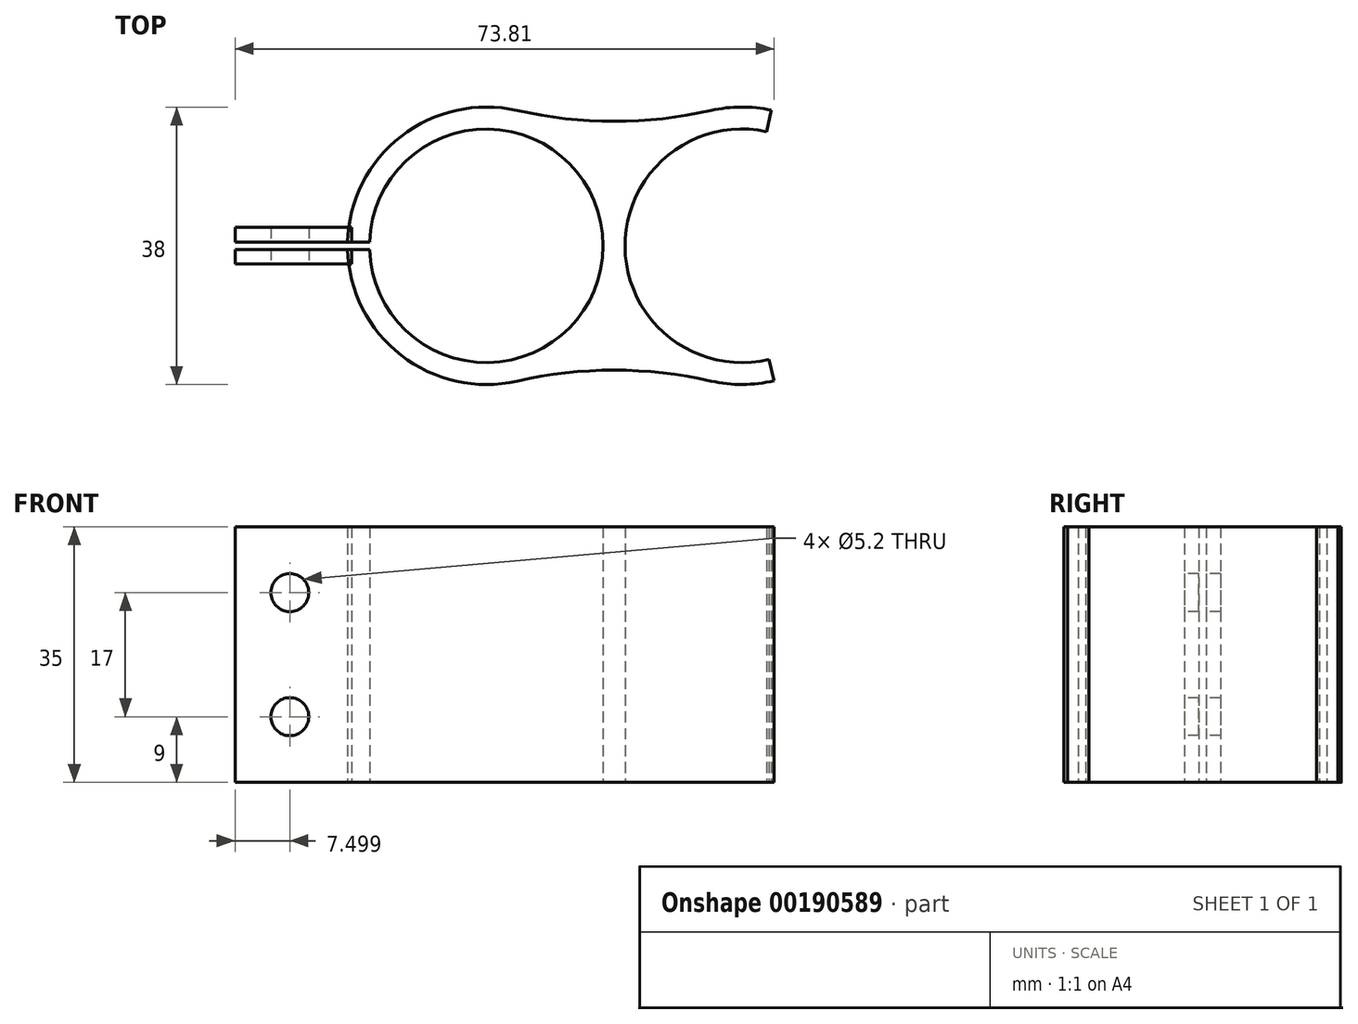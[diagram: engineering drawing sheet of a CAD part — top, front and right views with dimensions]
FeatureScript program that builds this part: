
annotation { "Feature Type Name" : "Feature", "Feature Type Description" : "" }
export const myFeature = defineFeature(function(context is Context, id is Id, definition is map)
    precondition{}
    {
        {
            var Q0;
            Q0=qCreatedBy(makeId("Top.planeOp"),FACE);
            var sketch = newSketch(context, id + "F0", { "sketchPlane" : qUnion([Q0])});
            skCircle(sketch, "E0", {"center": v(0, 0) * mm, "radius": 16 * mm});
            skArc(sketch, "E1.0", {"start": v(4.2, 18.53) * mm, "mid": v(-19, 0) * mm, "end": v(4.2, -18.53) * mm});
            skArc(sketch, "E2", {"start": v(38.38, 15.64) * mm, "mid": v(19, -0.16) * mm, "end": v(38.7, -15.56) * mm});
            skArc(sketch, "E3", {"start": v(38.64, 18.65) * mm, "mid": v(38.61, 18.65) * mm, "end": v(38.59, 18.66) * mm});
            skArc(sketch, "E4.trimOffspring", {"start": v(16, 0.26) * mm, "mid": v(16, 0) * mm, "end": v(16, -0.26) * mm});
            skArc(sketch, "E5.trimOffspring", {"start": v(19, -0.26) * mm, "mid": v(19, 0) * mm, "end": v(19, 0.26) * mm});
            skArc(sketch, "E6.2", {"start": v(39.02, 18.57) * mm, "mid": v(34.9, 19) * mm, "end": v(30.79, 18.53) * mm});
            skArc(sketch, "E7.trimOffspring", {"start": v(30.79, -18.53) * mm, "mid": v(35.1, -19) * mm, "end": v(39.4, -18.48) * mm});
            skPoint(sketch, "E8.visualSharp", {"position": v(17.5, 7.4) * mm});
            skArc(sketch, "E8.filletArc", {"start": v(4.2, 18.53) * mm, "mid": v(17.5, 17.04) * mm, "end": v(30.79, 18.53) * mm});
            skPoint(sketch, "E9.visualSharp", {"position": v(17.5, -7.4) * mm});
            skArc(sketch, "E9.filletArc", {"start": v(30.79, -18.53) * mm, "mid": v(17.5, -17.04) * mm, "end": v(4.2, -18.53) * mm});
            skLineSegment(sketch, "E10", {"start": v(38.38, 15.64) * mm, "end": v(39.02, 18.57) * mm});
            skLineSegment(sketch, "E11", {"start": v(38.7, -15.56) * mm, "end": v(39.4, -18.48) * mm});
            skSolve(sketch);
        }
        {
            var Q0;
            Q0=makeQuery(id+"F0.imprint","IMPRINT",FACE,{"disambiguationData":[TD([[makeQuery(id+"F0.imprint","IMPRINT",EDGE,{"derivedFrom":sQuery(id+"F0.wireOp",EDGE,"E1.0")}),1.0]])]});
            extrude(context, id + "F1", {"entities" : qUnion([Q0]), "depth" : 35 * mm});
        }
        {
            var Q0;
            Q0=qCreatedBy(makeId("Top.planeOp"),FACE);
            var sketch = newSketch(context, id + "F2", { "sketchPlane" : qUnion([Q0])});
            skLineSegment(sketch, "E12.bottom", {"start": v(-14.41, -0.5) * mm, "end": v(-22.41, -0.5) * mm});
            skLineSegment(sketch, "E12.top", {"start": v(-14.41, 0.5) * mm, "end": v(-22.41, 0.5) * mm});
            skLineSegment(sketch, "E12.left", {"start": v(-14.41, -0.5) * mm, "end": v(-14.41, 0.5) * mm});
            skLineSegment(sketch, "E12.right", {"start": v(-22.41, -0.5) * mm, "end": v(-22.41, 0.5) * mm});
            skPoint(sketch, "E12.middle", {"position": v(-18.41, 0) * mm});
            skLineSegment(sketch, "E13.bottom", {"start": v(-34.41, 2.5) * mm, "end": v(-18.41, 2.5) * mm});
            skLineSegment(sketch, "E13.top", {"start": v(-34.41, 0.5) * mm, "end": v(-18.41, 0.5) * mm});
            skLineSegment(sketch, "E13.left", {"start": v(-34.41, 2.5) * mm, "end": v(-34.41, 0.5) * mm});
            skLineSegment(sketch, "E13.right", {"start": v(-18.41, 2.5) * mm, "end": v(-18.41, 0.5) * mm});
            skLineSegment(sketch, "E14.bottom", {"start": v(-34.41, -0.5) * mm, "end": v(-18.41, -0.5) * mm});
            skLineSegment(sketch, "E14.top", {"start": v(-34.41, -2.5) * mm, "end": v(-18.41, -2.5) * mm});
            skLineSegment(sketch, "E14.left", {"start": v(-34.41, -0.5) * mm, "end": v(-34.41, -2.5) * mm});
            skLineSegment(sketch, "E14.right", {"start": v(-18.41, -0.5) * mm, "end": v(-18.41, -2.5) * mm});
            skSolve(sketch);
        }
        {
            var Q0;
            Q0=makeQuery(id+"F2.imprint","IMPRINT",FACE,{"disambiguationData":[TD([[makeQuery(id+"F2.imprint","IMPRINT",EDGE,{"derivedFrom":sQuery(id+"F2.wireOp",EDGE,"E12.bottom")}),-1.0]])]});
            extrude(context, id + "F3", {"entities" : qUnion([Q0]), "operationType" : NewBodyOperationType.REMOVE, "depth" : 40 * mm});
        }
        {
            var Q0;
            Q0=makeQuery(id+"F2.imprint","IMPRINT",FACE,{"disambiguationData":[TD([[makeQuery(id+"F2.imprint","IMPRINT",EDGE,{"derivedFrom":sQuery(id+"F2.wireOp",EDGE,"E13.bottom")}),-1.0]])]});
            var Q1;
            Q1=makeQuery(id+"F2.imprint","IMPRINT",FACE,{"disambiguationData":[TD([[makeQuery(id+"F2.imprint","IMPRINT",EDGE,{"derivedFrom":sQuery(id+"F2.wireOp",EDGE,"E14.top")}),1.0]])]});
            extrude(context, id + "F4", {"entities" : qUnion([Q0, Q1]), "depth" : 35 * mm});
        }
        {
            var Q0;
            Q0=qCreatedBy(makeId("Front.planeOp"),FACE);
            var sketch = newSketch(context, id + "F5", { "sketchPlane" : qUnion([Q0])});
            skCircle(sketch, "E15", {"center": v(-26.91, 26) * mm, "radius": 2.6 * mm});
            skCircle(sketch, "E16", {"center": v(-26.91, 9) * mm, "radius": 2.6 * mm});
            skSolve(sketch);
        }
        {
            var Q0;
            Q0 = qSketchRegion(id + "F5", true);
            extrude(context, id + "F6", {"entities" : qUnion([Q0]), "operationType" : NewBodyOperationType.REMOVE, "oppositeDirection" : true, "depth" : 25 * mm, "symmetric" : true});
        }
    });
